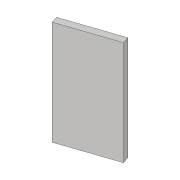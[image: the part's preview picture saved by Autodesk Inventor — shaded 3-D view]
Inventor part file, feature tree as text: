
AUTODESK INVENTOR PART (.ipt)
format: ipt  version: 2018.3 (Build 223284000, 284)  size: 72,192 bytes
history: native  units: in
note: dims shown in document units (in); Inventor stores cm internally (conversion verified against a paired STEP export)
features: extrude x1, sketch x1
ambient origin geometry x8: Origin, YZ Plane, XZ Plane, XY Plane, X Axis, Y Axis, Z Axis, Center Point
bodies: Solid1 (feature_tree)
feature tree (2):
  extrude  "Extrusion1"  Depth=1.925in TaperAngle=0.0deg
  sketch  "Sketch1"  dims[d0=1.04in d3=1.925in d4=0.0in]
